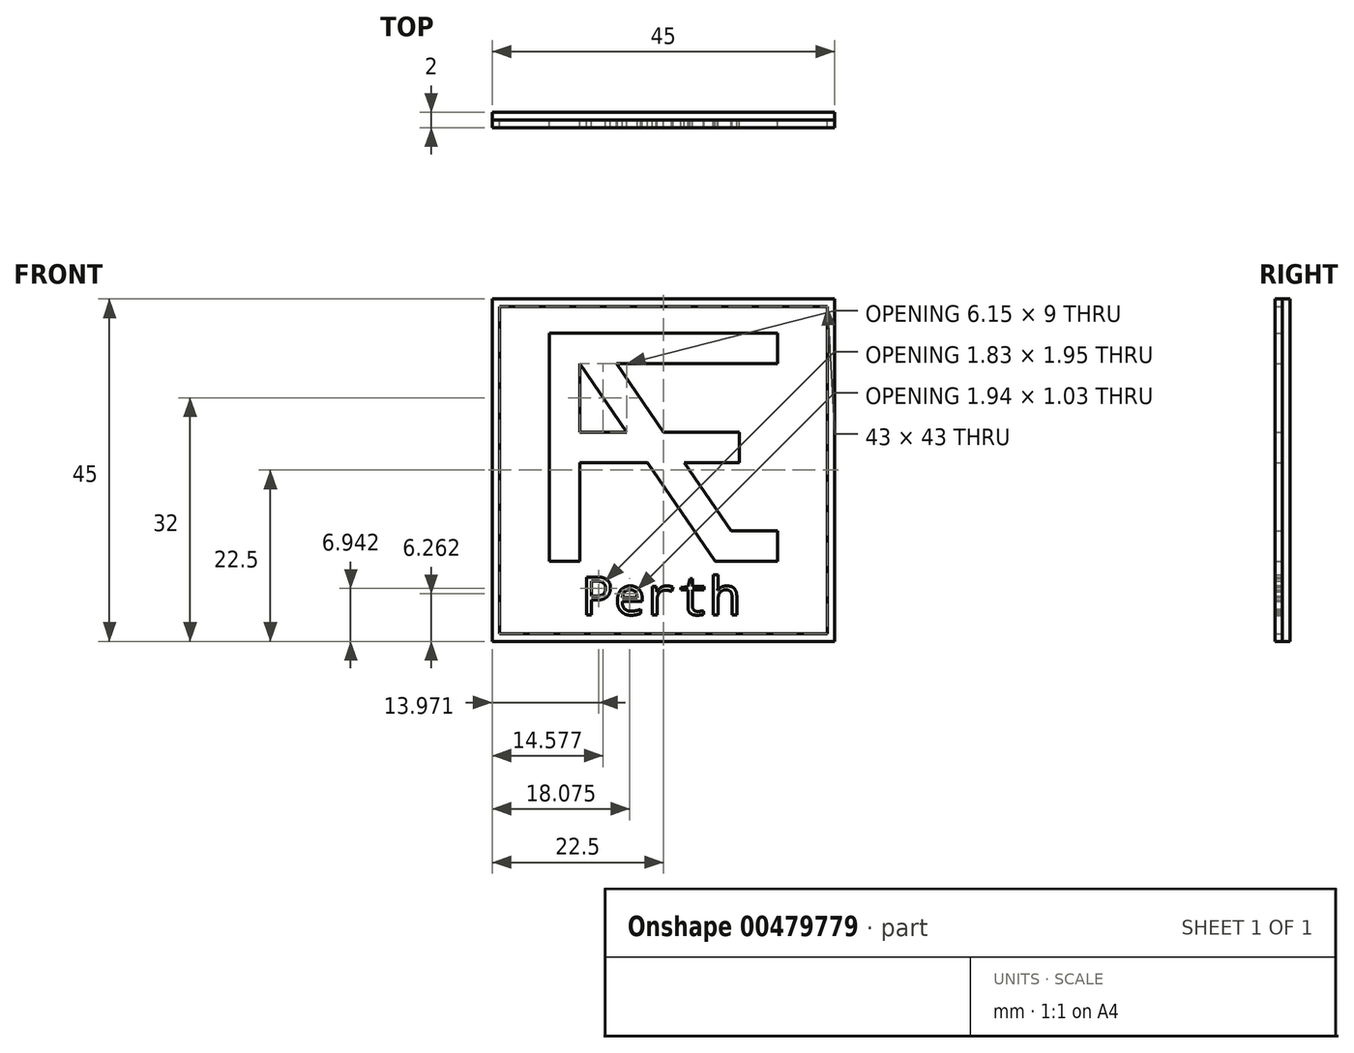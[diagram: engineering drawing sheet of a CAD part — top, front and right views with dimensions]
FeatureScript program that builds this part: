
annotation { "Feature Type Name" : "Feature", "Feature Type Description" : "" }
export const myFeature = defineFeature(function(context is Context, id is Id, definition is map)
    precondition{}
    {
        {
            var Q0;
            Q0=qCreatedBy(makeId("Front.planeOp"),FACE);
            var sketch = newSketch(context, id + "F0", { "sketchPlane" : qUnion([Q0])});
            skLineSegment(sketch, "E0.bottom", {"start": v(22.5, -25.5) * mm, "end": v(-22.5, -25.5) * mm});
            skLineSegment(sketch, "E0.top", {"start": v(22.5, 19.5) * mm, "end": v(-22.5, 19.5) * mm});
            skLineSegment(sketch, "E0.left", {"start": v(22.5, -25.5) * mm, "end": v(22.5, 19.5) * mm});
            skLineSegment(sketch, "E0.right", {"start": v(-22.5, -25.5) * mm, "end": v(-22.5, 19.5) * mm});
            skPoint(sketch, "E0.middle", {"position": v(0, -3) * mm});
            skSolve(sketch);
        }
        {
            var Q0;
            Q0=qSketchRegion(id+"F0",true);
            extrude(context, id + "F1", {"entities" : qUnion([Q0]), "depth" : 1 * mm});
        }
        {
            var Q0;
            Q0=qCreatedBy(makeId("Front.planeOp"),FACE);
            cPlane(context, id + "F2", {"entities" : qUnion([Q0]), "cplaneType" : CPlaneType.OFFSET, "offset" : 1 * mm, "width" : 150 * mm, "height" : 150 * mm});
        }
        {
            var Q0;
            Q0=qCreatedBy(id+"F2.planeOp",FACE);
            var sketch = newSketch(context, id + "F3", { "sketchPlane" : qUnion([Q0])});
            skLineSegment(sketch, "E1", {"start": v(-15, 15) * mm, "end": v(-15, -15) * mm});
            skLineSegment(sketch, "E2", {"start": v(-15, -15) * mm, "end": v(-11, -15) * mm});
            skLineSegment(sketch, "E3", {"start": v(-11, -15) * mm, "end": v(-11, -2) * mm});
            skLineSegment(sketch, "E4", {"start": v(-11, -2) * mm, "end": v(-2.11, -2) * mm});
            skLineSegment(sketch, "E5", {"start": v(-2.11, -2) * mm, "end": v(6.78, -15) * mm});
            skLineSegment(sketch, "E6", {"start": v(6.78, -15) * mm, "end": v(15, -15) * mm});
            skLineSegment(sketch, "E7", {"start": v(-15, 15) * mm, "end": v(15, 15) * mm});
            skLineSegment(sketch, "E8", {"start": v(15, 15) * mm, "end": v(15, 11) * mm});
            skLineSegment(sketch, "E9", {"start": v(15, 11) * mm, "end": v(-6.15, 11) * mm});
            skLineSegment(sketch, "E10", {"start": v(-6.15, 11) * mm, "end": v(0, 2) * mm});
            skLineSegment(sketch, "E11", {"start": v(0, 2) * mm, "end": v(10, 2) * mm});
            skLineSegment(sketch, "E12", {"start": v(10, 2) * mm, "end": v(10, -2) * mm});
            skLineSegment(sketch, "E13", {"start": v(10, -2) * mm, "end": v(2.74, -2) * mm});
            skLineSegment(sketch, "E14", {"start": v(2.74, -2) * mm, "end": v(8.89, -11) * mm});
            skLineSegment(sketch, "E15", {"start": v(8.89, -11) * mm, "end": v(15, -11) * mm});
            skLineSegment(sketch, "E16", {"start": v(-11, 2) * mm, "end": v(-11, 11) * mm});
            skLineSegment(sketch, "E17", {"start": v(-11, 11) * mm, "end": v(-4.85, 2) * mm});
            skLineSegment(sketch, "E18", {"start": v(-4.85, 2) * mm, "end": v(-11, 2) * mm});
            skLineSegment(sketch, "E19", {"start": v(15, -11) * mm, "end": v(15, -15) * mm});
            skText(sketch, "E20", { "text": "Perth", "fontName": "DroidSansMono.ttf"});
            skPoint(sketch, "E21.middle", {"position": v(0, 0) * mm});
            const initialGuessF3  = {"E20": [-0.01067, -0.022, 1, 0, 0.005]};
            skSetInitialGuess(sketch, initialGuessF3);
            skSolve(sketch);
        }
        {
            var Q0;
            Q0 = qSketchRegion(id + "F3", true);
            extrude(context, id + "F4", {"entities" : qUnion([Q0]), "depth" : 1 * mm});
        }
        {
            var Q0;
            Q0=qCreatedBy(id+"F2.planeOp",FACE);
            var sketch = newSketch(context, id + "F5", { "sketchPlane" : qUnion([Q0])});
            skLineSegment(sketch, "E22.bottom", {"start": v(-21.5, 18.5) * mm, "end": v(21.5, 18.5) * mm});
            skLineSegment(sketch, "E22.top", {"start": v(-21.5, -24.5) * mm, "end": v(21.5, -24.5) * mm});
            skLineSegment(sketch, "E22.left", {"start": v(-21.5, 18.5) * mm, "end": v(-21.5, -24.5) * mm});
            skLineSegment(sketch, "E22.right", {"start": v(21.5, 18.5) * mm, "end": v(21.5, -24.5) * mm});
            skPoint(sketch, "E22.middle", {"position": v(0, -3) * mm});
            skLineSegment(sketch, "E23.bottom", {"start": v(-22.5, 19.5) * mm, "end": v(22.5, 19.5) * mm});
            skLineSegment(sketch, "E23.top", {"start": v(-22.5, -25.5) * mm, "end": v(22.5, -25.5) * mm});
            skLineSegment(sketch, "E23.left", {"start": v(-22.5, 19.5) * mm, "end": v(-22.5, -25.5) * mm});
            skLineSegment(sketch, "E23.right", {"start": v(22.5, 19.5) * mm, "end": v(22.5, -25.5) * mm});
            skSolve(sketch);
        }
        {
            var Q0;
            Q0=qSketchRegion(id+"F5",true);
            extrude(context, id + "F6", {"entities" : qUnion([Q0]), "depth" : 1 * mm});
        }
    });
